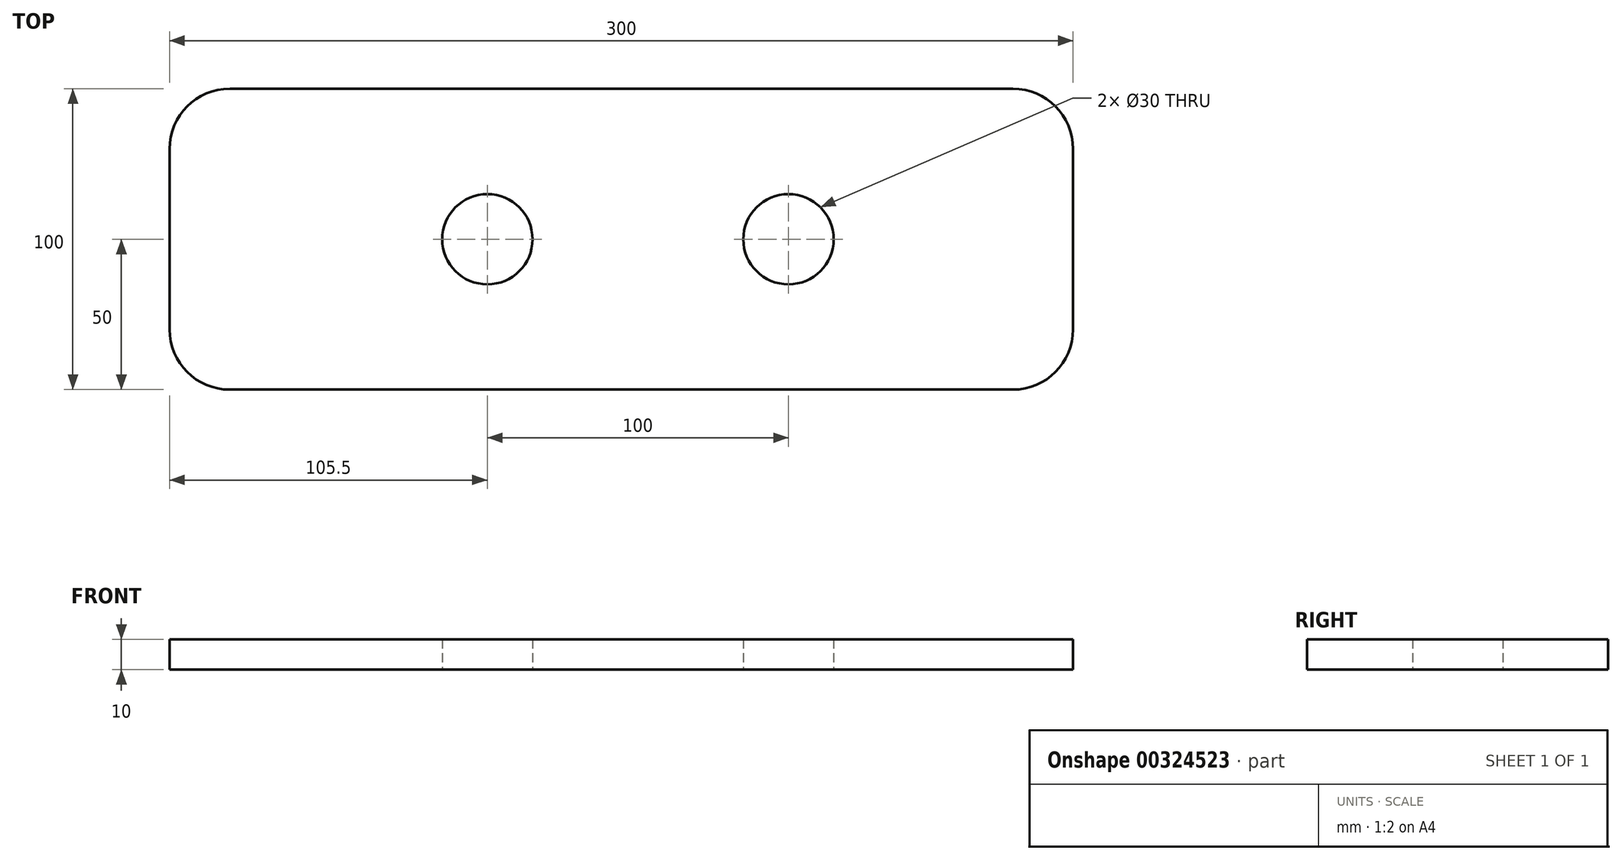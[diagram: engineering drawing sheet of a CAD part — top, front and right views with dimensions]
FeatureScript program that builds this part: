
annotation { "Feature Type Name" : "Feature", "Feature Type Description" : "" }
export const myFeature = defineFeature(function(context is Context, id is Id, definition is map)
    precondition{}
    {
        {
            var Q0;
            Q0=qCreatedBy(makeId("Top.planeOp"),FACE);
            var sketch = newSketch(context, id + "F0", { "sketchPlane" : qUnion([Q0])});
            skLineSegment(sketch, "E0.bottom", {"start": v(0, 0) * mm, "end": v(300, 0) * mm});
            skLineSegment(sketch, "E0.top", {"start": v(0, 100) * mm, "end": v(300, 100) * mm});
            skLineSegment(sketch, "E0.left", {"start": v(0, 0) * mm, "end": v(0, 100) * mm});
            skLineSegment(sketch, "E0.right", {"start": v(300, 0) * mm, "end": v(300, 100) * mm});
            skCircle(sketch, "E1", {"center": v(105.5, 50) * mm, "radius": 15 * mm});
            skCircle(sketch, "E2", {"center": v(205.5, 50) * mm, "radius": 15 * mm});
            skSolve(sketch);
        }
        {
            var Q0;
            Q0 = qSketchRegion(id + "F0", true);
            extrude(context, id + "F1", {"entities" : qUnion([Q0]), "depth" : 10 * mm});
        }
        {
            var Q0;
            Q0=makeQuery(id+"F1.opExtrude","SWEPT_EDGE",EDGE,{"disambiguationData":[OSD([sQuery(id+"F0.wireOp",EDGE,"E0.bottom"),sQuery(id+"F0.wireOp",EDGE,"E0.left")])]});
            var Q1;
            Q1=makeQuery(id+"F1.opExtrude","SWEPT_EDGE",EDGE,{"disambiguationData":[OSD([sQuery(id+"F0.wireOp",EDGE,"E0.top"),sQuery(id+"F0.wireOp",EDGE,"E0.left")])]});
            var Q2;
            Q2=makeQuery(id+"F1.opExtrude","SWEPT_EDGE",EDGE,{"disambiguationData":[OSD([sQuery(id+"F0.wireOp",EDGE,"E0.top"),sQuery(id+"F0.wireOp",EDGE,"E0.right")])]});
            var Q3;
            Q3=makeQuery(id+"F1.opExtrude","SWEPT_EDGE",EDGE,{"disambiguationData":[OSD([sQuery(id+"F0.wireOp",EDGE,"E0.bottom"),sQuery(id+"F0.wireOp",EDGE,"E0.right")])]});
            fillet(context, id + "F2", {"entities" : qUnion([Q0, Q1, Q2, Q3]), "radius" : 20 * mm, "tangentPropagation" : true, "allowEdgeOverflow" : false});
        }
    });
